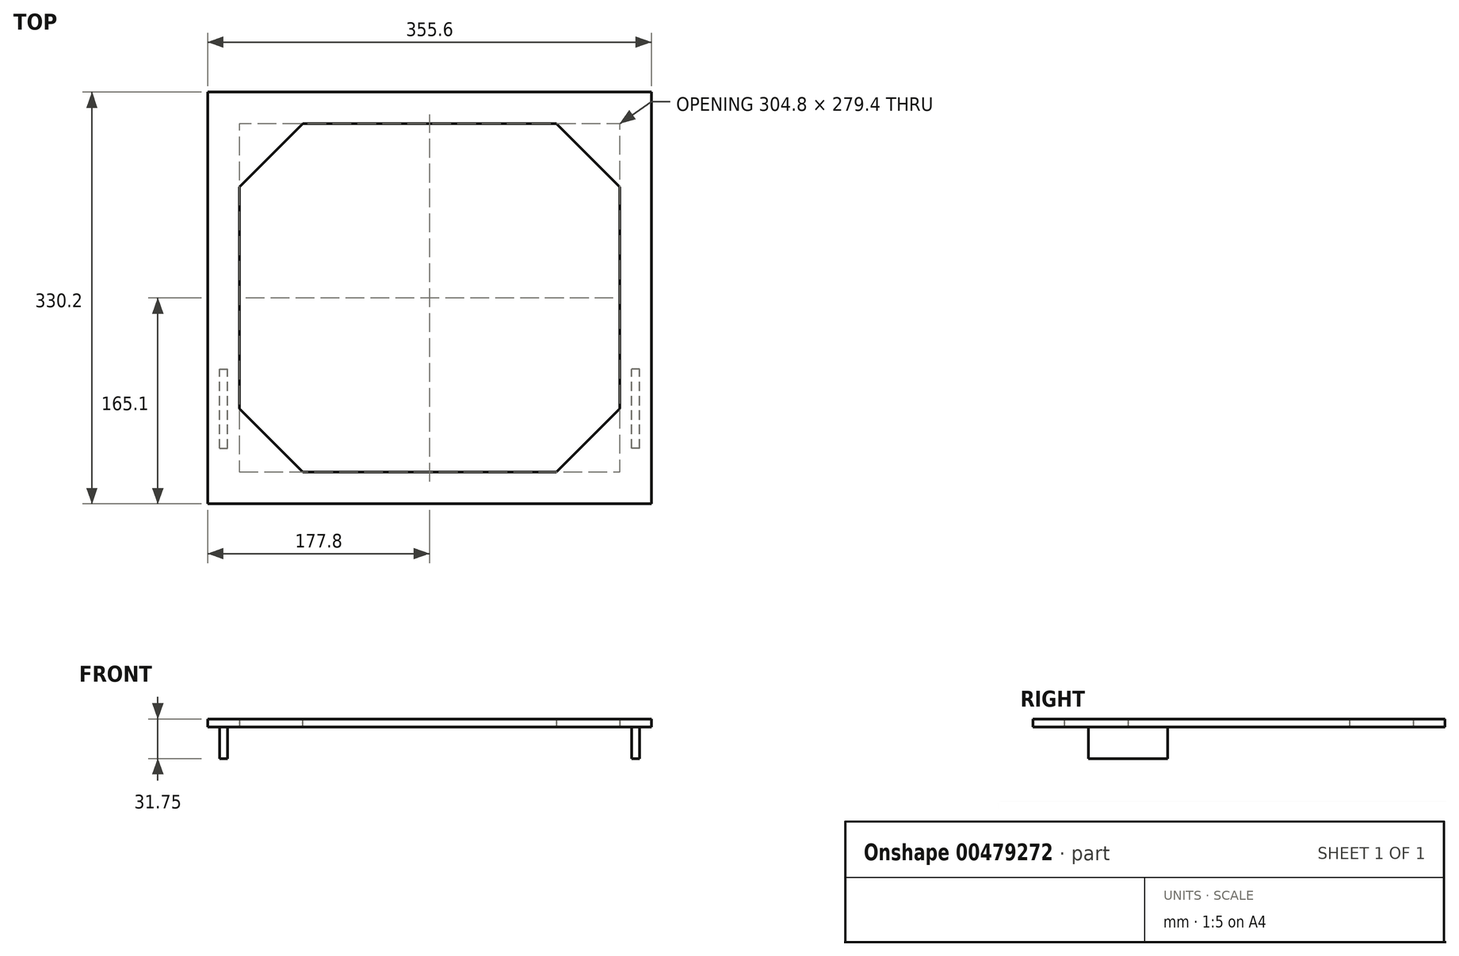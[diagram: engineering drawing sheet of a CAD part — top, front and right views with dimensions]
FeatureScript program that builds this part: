
annotation { "Feature Type Name" : "Feature", "Feature Type Description" : "" }
export const myFeature = defineFeature(function(context is Context, id is Id, definition is map)
    precondition{}
    {
        {
            var Q0;
            Q0=qCreatedBy(makeId("Top.planeOp"),FACE);
            var sketch = newSketch(context, id + "F0", { "sketchPlane" : qUnion([Q0])});
            skLineSegment(sketch, "E0.bottom", {"start": v(0, 0) * mm, "end": v(355.6, 0) * mm});
            skLineSegment(sketch, "E0.top", {"start": v(0, 330.2) * mm, "end": v(355.6, 330.2) * mm});
            skLineSegment(sketch, "E0.left", {"start": v(0, 0) * mm, "end": v(0, 330.2) * mm});
            skLineSegment(sketch, "E0.right", {"start": v(355.6, 0) * mm, "end": v(355.6, 330.2) * mm});
            skLineSegment(sketch, "E1.bottom", {"start": v(25.4, 25.4) * mm, "end": v(330.2, 25.4) * mm});
            skLineSegment(sketch, "E1.top", {"start": v(25.4, 304.8) * mm, "end": v(330.2, 304.8) * mm});
            skLineSegment(sketch, "E1.left", {"start": v(25.4, 25.4) * mm, "end": v(25.4, 304.8) * mm});
            skLineSegment(sketch, "E1.right", {"start": v(330.2, 25.4) * mm, "end": v(330.2, 304.8) * mm});
            skLineSegment(sketch, "E2.bottom", {"start": v(0, 0) * mm, "end": v(25.4, 0) * mm, "construction": true});
            skLineSegment(sketch, "E2.top", {"start": v(0, 25.4) * mm, "end": v(25.4, 25.4) * mm, "construction": true});
            skLineSegment(sketch, "E2.left", {"start": v(0, 0) * mm, "end": v(0, 25.4) * mm, "construction": true});
            skLineSegment(sketch, "E2.right", {"start": v(25.4, 0) * mm, "end": v(25.4, 25.4) * mm, "construction": true});
            skLineSegment(sketch, "E3.bottom", {"start": v(355.6, 330.2) * mm, "end": v(330.2, 330.2) * mm, "construction": true});
            skLineSegment(sketch, "E3.top", {"start": v(355.6, 304.8) * mm, "end": v(330.2, 304.8) * mm, "construction": true});
            skLineSegment(sketch, "E3.left", {"start": v(355.6, 330.2) * mm, "end": v(355.6, 304.8) * mm, "construction": true});
            skLineSegment(sketch, "E3.right", {"start": v(330.2, 330.2) * mm, "end": v(330.2, 304.8) * mm, "construction": true});
            skLineSegment(sketch, "E4.bottom", {"start": v(9.53, 50.8) * mm, "end": v(15.88, 50.8) * mm});
            skLineSegment(sketch, "E4.top", {"start": v(9.52, 101.6) * mm, "end": v(15.88, 101.6) * mm});
            skLineSegment(sketch, "E4.left", {"start": v(9.52, 50.8) * mm, "end": v(9.52, 101.6) * mm});
            skLineSegment(sketch, "E4.right", {"start": v(15.87, 50.8) * mm, "end": v(15.87, 101.6) * mm});
            skLineSegment(sketch, "E5", {"start": v(177.8, -169.94) * mm, "end": v(177.8, 419.49) * mm, "construction": true});
            skLineSegment(sketch, "E6.MirrorCS", {"start": v(346.08, 50.8) * mm, "end": v(339.73, 50.8) * mm});
            skLineSegment(sketch, "E7.MirrorCS", {"start": v(339.73, 50.8) * mm, "end": v(339.73, 101.6) * mm});
            skLineSegment(sketch, "E8.MirrorCS", {"start": v(346.08, 50.8) * mm, "end": v(346.08, 101.6) * mm});
            skLineSegment(sketch, "E9.MirrorCS", {"start": v(346.08, 101.6) * mm, "end": v(339.73, 101.6) * mm});
            skLineSegment(sketch, "E10.bottom", {"start": v(9.52, 44.45) * mm, "end": v(15.88, 44.45) * mm});
            skLineSegment(sketch, "E10.top", {"start": v(9.52, 107.95) * mm, "end": v(15.87, 107.95) * mm});
            skLineSegment(sketch, "E10.left", {"start": v(9.52, 44.45) * mm, "end": v(9.52, 107.95) * mm});
            skLineSegment(sketch, "E10.right", {"start": v(15.88, 44.45) * mm, "end": v(15.87, 107.95) * mm});
            skLineSegment(sketch, "E11.MirrorCS", {"start": v(346.08, 44.45) * mm, "end": v(339.73, 44.45) * mm});
            skLineSegment(sketch, "E12.MirrorCS", {"start": v(339.72, 44.45) * mm, "end": v(339.72, 107.95) * mm});
            skLineSegment(sketch, "E13.MirrorCS", {"start": v(346.07, 44.45) * mm, "end": v(346.07, 107.95) * mm});
            skLineSegment(sketch, "E14.MirrorCS", {"start": v(346.08, 107.95) * mm, "end": v(339.73, 107.95) * mm});
            skSolve(sketch);
        }
        {
            var Q0;
            Q0 = qSketchRegion(id + "F0", true);
            var Q1;
            Q1=makeQuery(id+"F0.imprint","IMPRINT",FACE,{"disambiguationData":[TD([[makeQuery(id+"F0.imprint","IMPRINT",EDGE,{"derivedFrom":sQuery(id+"F0.wireOp",EDGE,"E4.bottom")}),-1.0]])]});
            var Q2;
            Q2=makeQuery(id+"F0.imprint","IMPRINT",FACE,{"disambiguationData":[TD([[makeQuery(id+"F0.imprint","IMPRINT",EDGE,{"derivedFrom":sQuery(id+"F0.wireOp",EDGE,"E6.MirrorCS")}),1.0]])]});
            var Q3;
            {var subQ0=sQuery(id+"F0.wireOp",EDGE,"E9.MirrorCS");Q3=makeQuery(id+"F0.imprint","IMPRINT",FACE,{"disambiguationData":[TD([[makeQuery(id+"F0.imprint","IMPRINT",EDGE,{"derivedFrom":subQ0}),-1.0]])]});}
            var Q4;
            {var subQ0=sQuery(id+"F0.wireOp",EDGE,"E4.top");Q4=makeQuery(id+"F0.imprint","IMPRINT",FACE,{"disambiguationData":[TD([[makeQuery(id+"F0.imprint","IMPRINT",EDGE,{"derivedFrom":subQ0}),1.0]])]});}
            extrude(context, id + "F1", {"entities" : qUnion([Q0, Q1, Q2, Q3, Q4]), "depth" : 6.35 * mm});
        }
        {
            var Q0;
            Q0=makeQuery(id+"F1.opExtrude","SWEPT_EDGE",EDGE,{"disambiguationData":[OSD([sQuery(id+"F0.wireOp",EDGE,"E1.top"),sQuery(id+"F0.wireOp",EDGE,"E1.left")])]});
            var Q1;
            Q1=makeQuery(id+"F1.opExtrude","SWEPT_EDGE",EDGE,{"disambiguationData":[OSD([sQuery(id+"F0.wireOp",EDGE,"E1.bottom"),sQuery(id+"F0.wireOp",EDGE,"E1.left")])]});
            var Q2;
            Q2=makeQuery(id+"F1.opExtrude","SWEPT_EDGE",EDGE,{"disambiguationData":[OSD([sQuery(id+"F0.wireOp",EDGE,"E1.bottom"),sQuery(id+"F0.wireOp",EDGE,"E1.right")])]});
            var Q3;
            Q3=makeQuery(id+"F1.opExtrude","SWEPT_EDGE",EDGE,{"disambiguationData":[OSD([sQuery(id+"F0.wireOp",EDGE,"E1.top"),sQuery(id+"F0.wireOp",EDGE,"E1.right")])]});
            chamfer(context, id + "F2", {"entities" : qUnion([Q0, Q1, Q2, Q3]), "width" : 50.8 * mm, "tangentPropagation" : true});
        }
        {
            var Q0;
            Q0=makeQuery(id+"F0.imprint","IMPRINT",FACE,{"disambiguationData":[TD([[makeQuery(id+"F0.imprint","IMPRINT",EDGE,{"derivedFrom":sQuery(id+"F0.wireOp",EDGE,"E4.bottom")}),1.0]])]});
            var Q1;
            Q1=makeQuery(id+"F0.imprint","IMPRINT",FACE,{"disambiguationData":[TD([[makeQuery(id+"F0.imprint","IMPRINT",EDGE,{"derivedFrom":sQuery(id+"F0.wireOp",EDGE,"E6.MirrorCS")}),-1.0]])]});
            var Q2;
            Q2=makeQuery(id+"F1.opExtrude","CAP_FACE",FACE,{"disambiguationData":[OSD([sQuery(id+"F0.wireOp",EDGE,"E0.bottom"),sQuery(id+"F0.wireOp",EDGE,"E0.top"),sQuery(id+"F0.wireOp",EDGE,"E0.left"),sQuery(id+"F0.wireOp",EDGE,"E0.right"),sQuery(id+"F0.wireOp",EDGE,"E1.bottom"),sQuery(id+"F0.wireOp",EDGE,"E1.top"),sQuery(id+"F0.wireOp",EDGE,"E1.left"),sQuery(id+"F0.wireOp",EDGE,"E1.right"),sQuery(id+"F0.wireOp",EDGE,"E4.bottom"),sQuery(id+"F0.wireOp",EDGE,"E4.top"),sQuery(id+"F0.wireOp",EDGE,"E4.left"),sQuery(id+"F0.wireOp",EDGE,"E4.right"),sQuery(id+"F0.wireOp",EDGE,"E6.MirrorCS"),sQuery(id+"F0.wireOp",EDGE,"E7.MirrorCS"),sQuery(id+"F0.wireOp",EDGE,"E8.MirrorCS"),sQuery(id+"F0.wireOp",EDGE,"E9.MirrorCS")])],"isStart":false});
            extrude(context, id + "F3", {"entities" : qUnion([Q0, Q1]), "endBound" : BoundingType.UP_TO_SURFACE, "endBoundEntityFace" : qUnion([Q2]), "depth" : 25.4 * mm});
        }
        {
            var Q0;
            Q0=makeQuery(id+"F0.imprint","IMPRINT",FACE,{"disambiguationData":[TD([[makeQuery(id+"F0.imprint","IMPRINT",EDGE,{"derivedFrom":sQuery(id+"F0.wireOp",EDGE,"E4.bottom")}),-1.0]])]});
            var Q1;
            Q1=makeQuery(id+"F0.imprint","IMPRINT",FACE,{"disambiguationData":[TD([[makeQuery(id+"F0.imprint","IMPRINT",EDGE,{"derivedFrom":sQuery(id+"F0.wireOp",EDGE,"E6.MirrorCS")}),1.0]])]});
            var Q2;
            Q2=makeQuery(id+"F0.imprint","IMPRINT",FACE,{"disambiguationData":[TD([[makeQuery(id+"F0.imprint","IMPRINT",EDGE,{"derivedFrom":sQuery(id+"F0.wireOp",EDGE,"E4.bottom")}),1.0]])]});
            var Q3;
            Q3=makeQuery(id+"F0.imprint","IMPRINT",FACE,{"disambiguationData":[TD([[makeQuery(id+"F0.imprint","IMPRINT",EDGE,{"derivedFrom":sQuery(id+"F0.wireOp",EDGE,"E6.MirrorCS")}),-1.0]])]});
            var Q4;
            {var subQ0=sQuery(id+"F0.wireOp",EDGE,"E4.top");Q4=makeQuery(id+"F0.imprint","IMPRINT",FACE,{"disambiguationData":[TD([[makeQuery(id+"F0.imprint","IMPRINT",EDGE,{"derivedFrom":subQ0}),1.0]])]});}
            var Q5;
            {var subQ0=sQuery(id+"F0.wireOp",EDGE,"E9.MirrorCS");Q5=makeQuery(id+"F0.imprint","IMPRINT",FACE,{"disambiguationData":[TD([[makeQuery(id+"F0.imprint","IMPRINT",EDGE,{"derivedFrom":subQ0}),-1.0]])]});}
            extrude(context, id + "F4", {"entities" : qUnion([Q0, Q1, Q2, Q3, Q4, Q5]), "operationType" : NewBodyOperationType.ADD, "oppositeDirection" : true, "depth" : 25.4 * mm});
        }
    });
